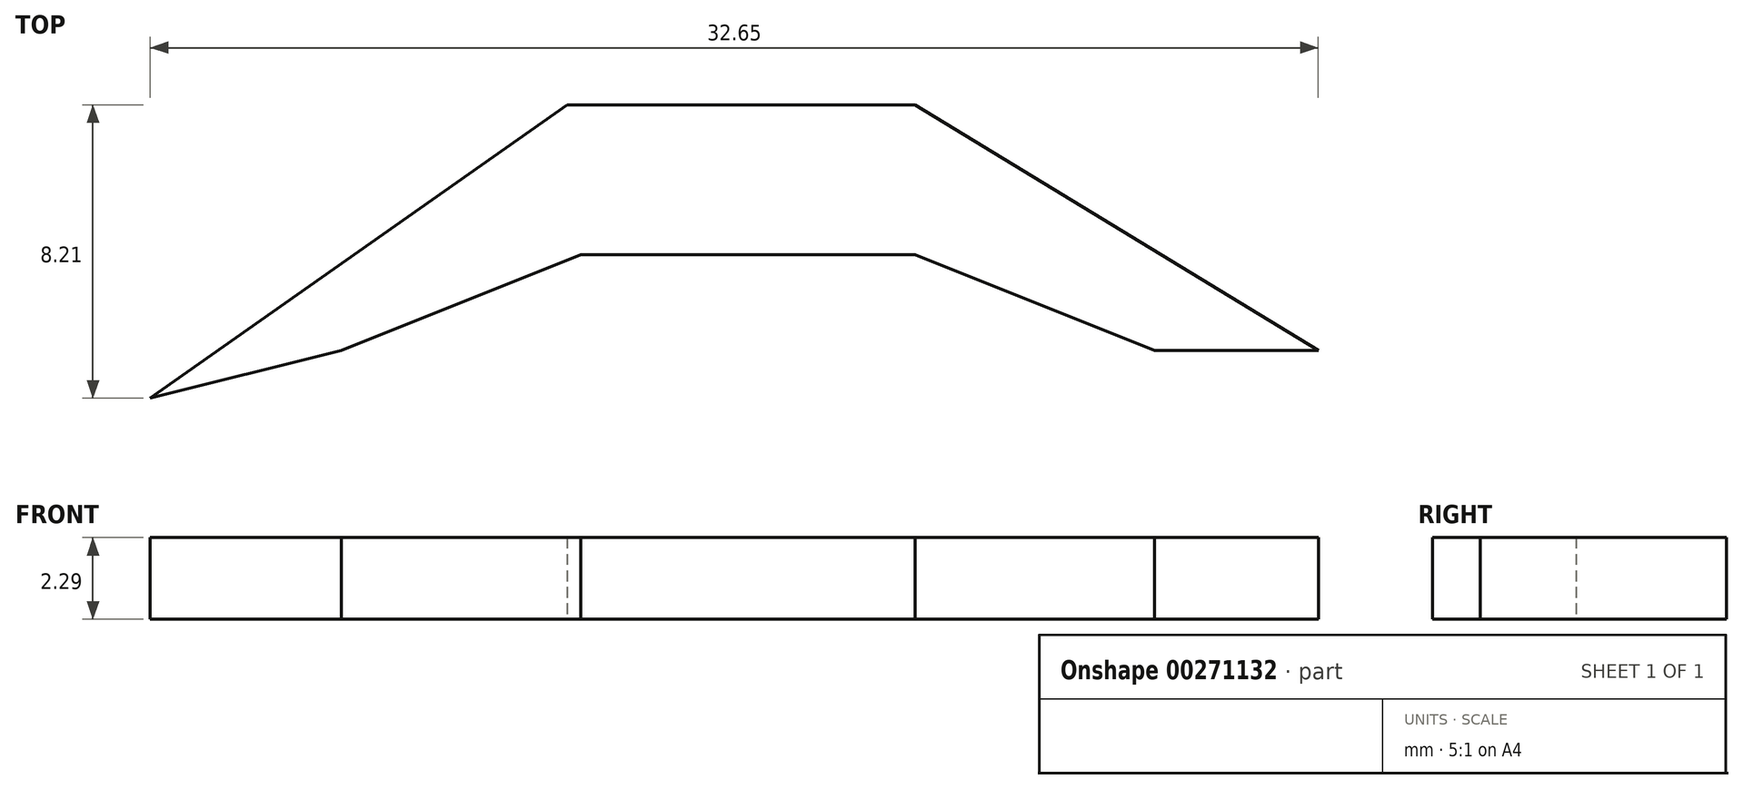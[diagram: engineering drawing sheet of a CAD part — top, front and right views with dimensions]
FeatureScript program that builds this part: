
annotation { "Feature Type Name" : "Feature", "Feature Type Description" : "" }
export const myFeature = defineFeature(function(context is Context, id is Id, definition is map)
    precondition{}
    {
        {
            var Q0;
            Q0=qCreatedBy(makeId("Top.planeOp"),FACE);
            var sketch = newSketch(context, id + "F0", { "sketchPlane" : qUnion([Q0])});
            skLineSegment(sketch, "E0", {"start": v(-51.94, -4.01) * mm, "end": v(-40.3, 4.2) * mm});
            skLineSegment(sketch, "E1", {"start": v(-40.3, 4.2) * mm, "end": v(-30.55, 4.2) * mm});
            skLineSegment(sketch, "E2", {"start": v(-30.55, 4.2) * mm, "end": v(-19.29, -2.67) * mm});
            skLineSegment(sketch, "E3", {"start": v(-19.29, -2.67) * mm, "end": v(-23.87, -2.67) * mm});
            skLineSegment(sketch, "E4", {"start": v(-23.87, -2.67) * mm, "end": v(-30.55, 0) * mm});
            skLineSegment(sketch, "E5", {"start": v(-30.55, 0) * mm, "end": v(-39.9, 0) * mm});
            skLineSegment(sketch, "E6", {"start": v(-39.9, 0) * mm, "end": v(-46.6, -2.67) * mm});
            skLineSegment(sketch, "E7", {"start": v(-46.6, -2.67) * mm, "end": v(-51.94, -4.01) * mm});
            skSolve(sketch);
        }
        {
            var Q0;
            Q0 = qSketchRegion(id + "F0", true);
            extrude(context, id + "F1", {"entities" : qUnion([Q0]), "depth" : 2.3 * mm});
        }
    });
